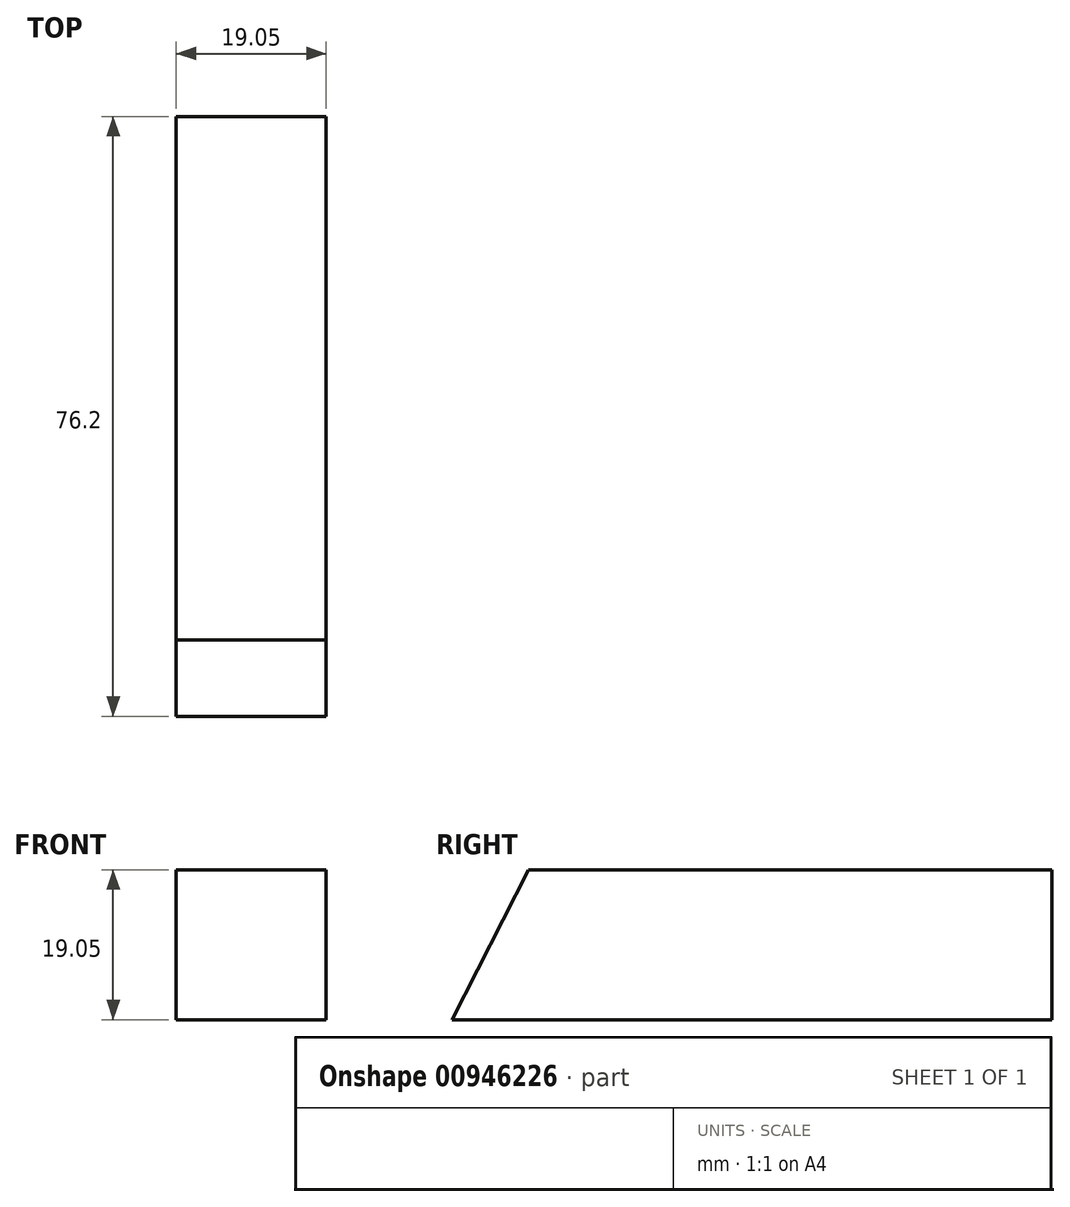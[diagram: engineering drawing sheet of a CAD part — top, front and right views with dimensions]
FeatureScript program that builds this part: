
annotation { "Feature Type Name" : "Feature", "Feature Type Description" : "" }
export const myFeature = defineFeature(function(context is Context, id is Id, definition is map)
    precondition{}
    {
        {
            var Q0;
            Q0=qCreatedBy(makeId("Front.planeOp"),FACE);
            var sketch = newSketch(context, id + "F0", { "sketchPlane" : qUnion([Q0])});
            skLineSegment(sketch, "E0.bottom", {"start": v(0, 0) * mm, "end": v(19.05, 0) * mm});
            skLineSegment(sketch, "E0.top", {"start": v(0, 19.05) * mm, "end": v(19.05, 19.05) * mm});
            skLineSegment(sketch, "E0.left", {"start": v(0, 0) * mm, "end": v(0, 19.05) * mm});
            skLineSegment(sketch, "E0.right", {"start": v(19.05, 0) * mm, "end": v(19.05, 19.05) * mm});
            skSolve(sketch);
        }
        {
            var Q0;
            Q0 = qSketchRegion(id + "F0", true);
            extrude(context, id + "F1", {"entities" : qUnion([Q0]), "depth" : 76.2 * mm, "offsetDistance" : 25.4 * mm});
        }
        {
            var Q0;
            Q0=makeQuery(id+"F1.opExtrude","SWEPT_FACE",FACE,{"disambiguationData":[OSD([sQuery(id+"F0.wireOp",EDGE,"E0.left")])]});
            var sketch = newSketch(context, id + "F2", { "sketchPlane" : qUnion([Q0])});
            skLineSegment(sketch, "E1", {"start": v(66.5, 19.05) * mm, "end": v(76.2, 0) * mm});
            skSolve(sketch);
        }
        {
            var Q0;
            {var subQ0=sQuery(id+"F2.wireOp",EDGE,"E1");Q0=makeQuery(id+"F2.imprint","IMPRINT",FACE,{"disambiguationData":[TD([[makeQuery(id+"F2.imprint","IMPRINT",EDGE,{"derivedFrom":subQ0}),1.0]])]});}
            extrude(context, id + "F3", {"entities" : qUnion([Q0]), "operationType" : NewBodyOperationType.REMOVE, "oppositeDirection" : true, "depth" : 25.4 * mm, "offsetDistance" : 25.4 * mm});
        }
    });
